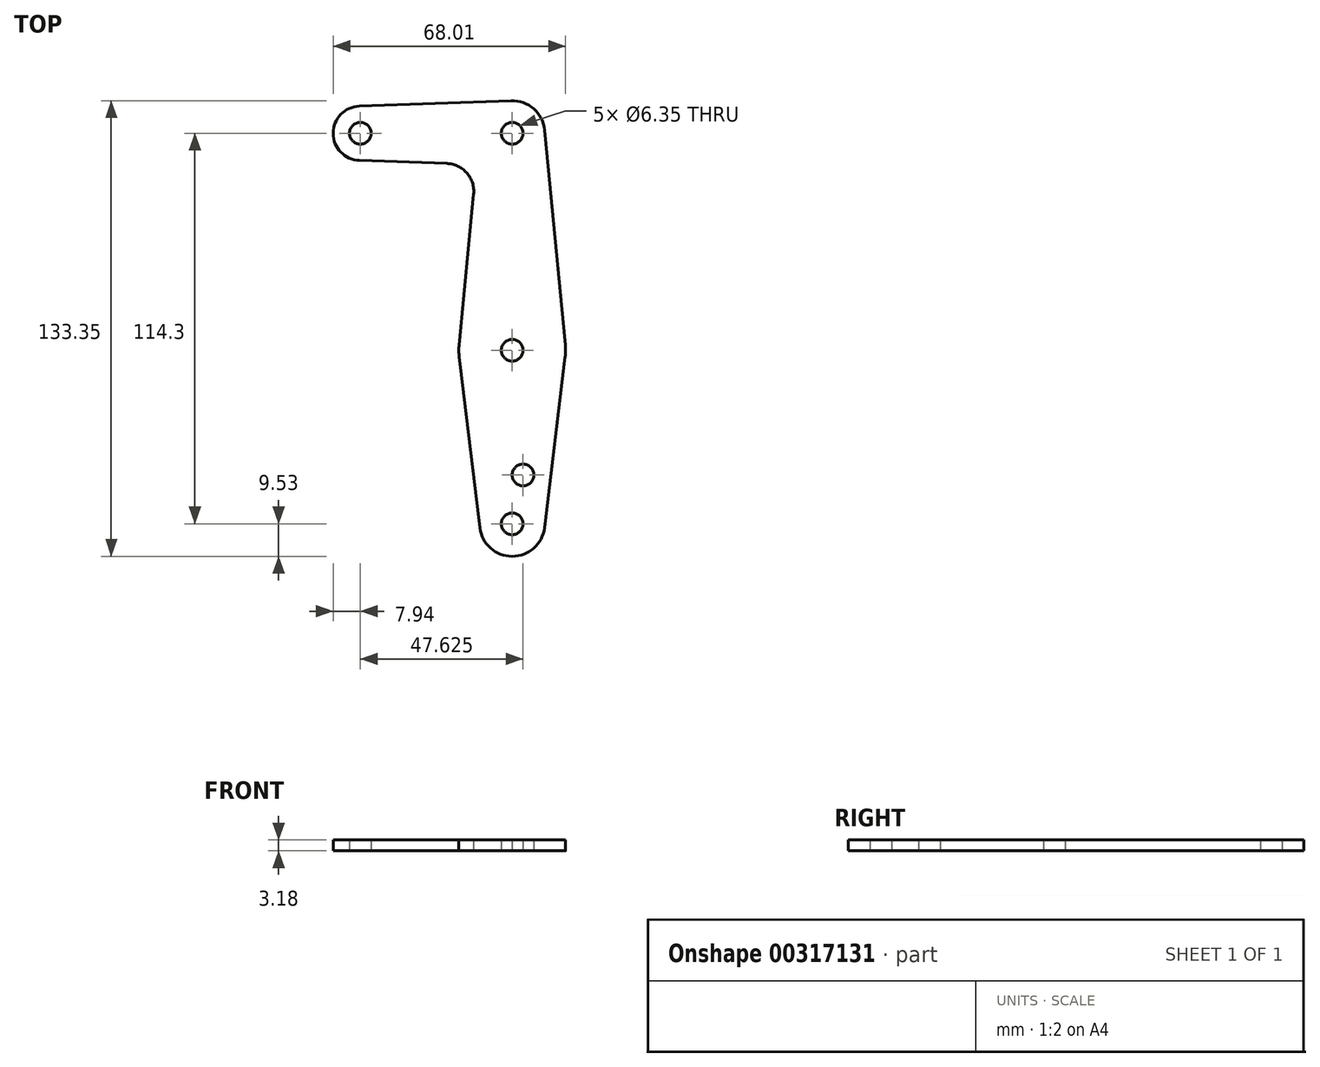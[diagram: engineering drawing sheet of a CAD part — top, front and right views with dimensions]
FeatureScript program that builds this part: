
annotation { "Feature Type Name" : "Feature", "Feature Type Description" : "" }
export const myFeature = defineFeature(function(context is Context, id is Id, definition is map)
    precondition{}
    {
        {
            var Q0;
            Q0=qCreatedBy(makeId("Top.planeOp"),FACE);
            var sketch = newSketch(context, id + "F0", { "sketchPlane" : qUnion([Q0])});
            skCircle(sketch, "E0", {"center": v(-44.45, 0) * mm, "radius": 3.18 * mm});
            skCircle(sketch, "E1", {"center": v(0, 0) * mm, "radius": 3.18 * mm});
            skCircle(sketch, "E2", {"center": v(0, -63.5) * mm, "radius": 3.18 * mm});
            skCircle(sketch, "E3", {"center": v(0, -114.3) * mm, "radius": 3.18 * mm});
            skCircle(sketch, "E4", {"center": v(3.17, -100.01) * mm, "radius": 3.18 * mm});
            skCircle(sketch, "E5", {"center": v(-44.45, 0) * mm, "radius": 7.94 * mm});
            skCircle(sketch, "E6", {"center": v(0, -63.5) * mm, "radius": 15.62 * mm});
            skCircle(sketch, "E7", {"center": v(0, -114.3) * mm, "radius": 9.53 * mm});
            skPoint(sketch, "E8.orphan", {"position": v(0, 16.2) * mm});
            skLineSegment(sketch, "E9", {"start": v(15.5, -65.37) * mm, "end": v(9.46, -115.44) * mm});
            skLineSegment(sketch, "E10", {"start": v(-9.46, -115.44) * mm, "end": v(-15.5, -65.37) * mm});
            skCircle(sketch, "E11", {"center": v(0, 0) * mm, "radius": 9.53 * mm});
            skLineSegment(sketch, "E12", {"start": v(9.48, 0.91) * mm, "end": v(15.55, -62) * mm});
            skLineSegment(sketch, "E13", {"start": v(-0.34, 9.52) * mm, "end": v(-44.73, 7.93) * mm});
            skPoint(sketch, "E14.endSnap0", {"position": v(12.51, -30.54) * mm});
            skPoint(sketch, "E15.orphan", {"position": v(587.96, -30.54) * mm});
            skLineSegment(sketch, "E16", {"start": v(-9.48, 0.91) * mm, "end": v(-15.55, -62) * mm});
            skLineSegment(sketch, "E17", {"start": v(-44.73, -7.93) * mm, "end": v(-0.34, -9.52) * mm});
            skSolve(sketch);
        }
        {
            var Q0;
            Q0=qSketchRegion(id+"F0",true);
            extrude(context, id + "F1", {"entities" : qUnion([Q0]), "depth" : 3.17 * mm});
        }
        {
            var Q0;
            Q0=makeQuery(id+"F1.opExtrude","SWEPT_EDGE",EDGE,{"disambiguationData":[OSD([sQuery(id+"F0.wireOp",EDGE,"E16"),sQuery(id+"F0.wireOp",EDGE,"E17")])]});
            fillet(context, id + "F2", {"entities" : qUnion([Q0]), "radius" : 8.2 * mm, "tangentPropagation" : true, "allowEdgeOverflow" : false});
        }
    });
